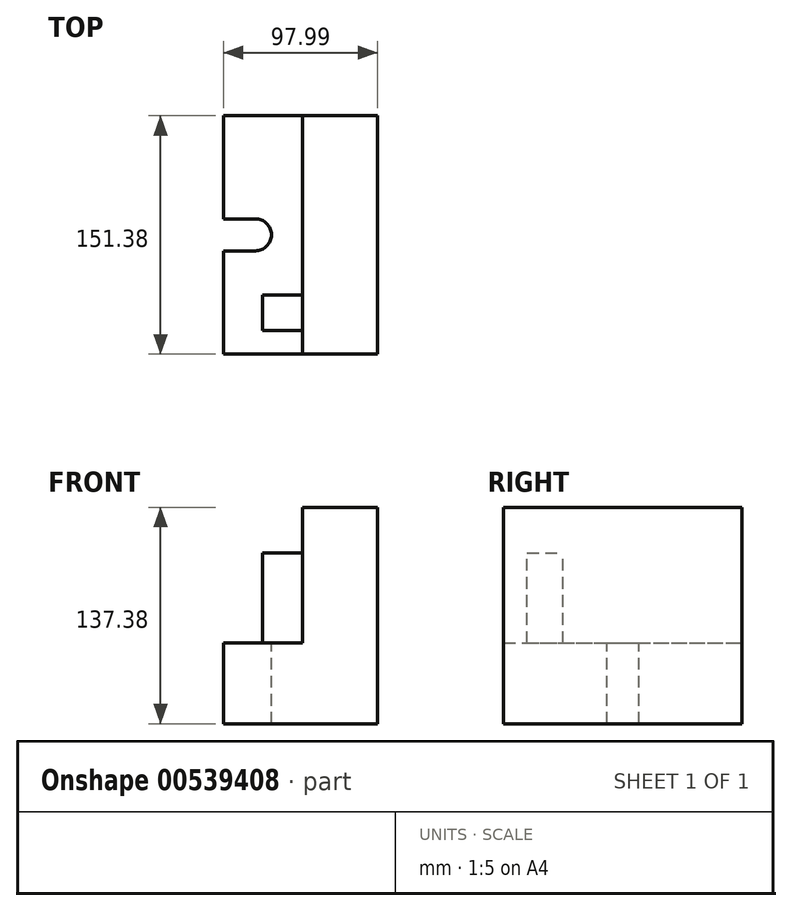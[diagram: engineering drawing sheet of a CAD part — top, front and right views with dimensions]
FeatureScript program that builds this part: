
annotation { "Feature Type Name" : "Feature", "Feature Type Description" : "" }
export const myFeature = defineFeature(function(context is Context, id is Id, definition is map)
    precondition{}
    {
        {
            var Q0;
            Q0=qCreatedBy(makeId("Front.planeOp"),FACE);
            var sketch = newSketch(context, id + "F0", { "sketchPlane" : qUnion([Q0])});
            skLineSegment(sketch, "E0.bottom", {"start": v(23.81, -68.69) * mm, "end": v(-23.81, -68.69) * mm});
            skLineSegment(sketch, "E0.top", {"start": v(23.81, 68.69) * mm, "end": v(-23.81, 68.69) * mm});
            skLineSegment(sketch, "E0.left", {"start": v(23.81, -68.69) * mm, "end": v(23.81, 68.69) * mm});
            skLineSegment(sketch, "E0.right", {"start": v(-23.81, -17.4) * mm, "end": v(-23.81, 68.69) * mm});
            skPoint(sketch, "E0.middle", {"position": v(0, 0) * mm});
            skLineSegment(sketch, "E1.bottom", {"start": v(23.81, -68.69) * mm, "end": v(-74.18, -68.69) * mm});
            skLineSegment(sketch, "E1.top", {"start": v(-23.81, -17.4) * mm, "end": v(-74.18, -17.4) * mm});
            skLineSegment(sketch, "E1.left", {"start": v(23.81, -68.69) * mm, "end": v(23.81, -17.4) * mm});
            skLineSegment(sketch, "E1.right", {"start": v(-74.18, -68.69) * mm, "end": v(-74.18, -17.4) * mm});
            skSolve(sketch);
        }
        {
            var Q0;
            Q0 = qSketchRegion(id + "F0", true);
            extrude(context, id + "F1", {"entities" : qUnion([Q0]), "endBound" : BoundingType.SYMMETRIC, "depth" : 151.38 * mm, "offsetDistance" : 25.4 * mm});
        }
        {
            var Q0;
            Q0=makeQuery(id+"F1.opExtrude","SWEPT_FACE",FACE,{"disambiguationData":[OSD([sQuery(id+"F0.wireOp",EDGE,"E1.top")])]});
            var sketch = newSketch(context, id + "F2", { "sketchPlane" : qUnion([Q0])});
            skCircle(sketch, "E2", {"center": v(-53.86, 0) * mm, "radius": 10.16 * mm});
            skLineSegment(sketch, "E3", {"start": v(-53.86, 10.16) * mm, "end": v(-74.18, 10.16) * mm});
            skLineSegment(sketch, "E4", {"start": v(-53.86, -10.16) * mm, "end": v(-74.18, -10.16) * mm});
            skLineSegment(sketch, "E5", {"start": v(-74.18, 10.16) * mm, "end": v(-74.18, -10.16) * mm});
            skSolve(sketch);
        }
        {
            var Q0;
            Q0 = qSketchRegion(id + "F2", true);
            extrude(context, id + "F3", {"entities" : qUnion([Q0]), "operationType" : NewBodyOperationType.REMOVE, "endBound" : BoundingType.THROUGH_ALL, "oppositeDirection" : true, "depth" : 25.4 * mm, "offsetDistance" : 25.4 * mm});
        }
        {
            var Q0;
            Q0=makeQuery(id+"F1.opExtrude","SWEPT_FACE",FACE,{"disambiguationData":[OSD([sQuery(id+"F0.wireOp",EDGE,"E0.right")])]});
            var sketch = newSketch(context, id + "F4", { "sketchPlane" : qUnion([Q0])});
            skLineSegment(sketch, "E6.bottom", {"start": v(60.75, -17.4) * mm, "end": v(38.16, -17.4) * mm});
            skLineSegment(sketch, "E6.top", {"start": v(60.75, 40) * mm, "end": v(38.16, 40) * mm});
            skLineSegment(sketch, "E6.left", {"start": v(60.75, -17.4) * mm, "end": v(60.75, 40) * mm});
            skLineSegment(sketch, "E6.right", {"start": v(38.16, -17.4) * mm, "end": v(38.16, 40) * mm});
            skSolve(sketch);
        }
        {
            var Q0;
            Q0 = qSketchRegion(id + "F4", true);
            extrude(context, id + "F5", {"entities" : qUnion([Q0]), "operationType" : NewBodyOperationType.ADD, "depth" : 25.4 * mm, "offsetDistance" : 25.4 * mm});
        }
    });
